# Revit family: Hager-Univers-IP65-D300-H550-Cl.II-encl-PT-pt
name_source: partatom
category: Equipement électrique
units: mm (PartAtom-declared; Revit-internal decimal feet)

## family parameters
Configuration du panneau = Deux colonnes, circuits au sein
Cote de connecteur circulaire = Utiliser le diamètre
Couper avec des vides une fois chargée = Non
Hôte = Face
Partagée = Non
Point de calcul de pièce = Non
Type d'élément = Tableau de raccordement

## types (6) — shared parameters
Commentaires du type = Univers
EF000003 - Método de montagem = EV000384 - Montagem em superfície (gesso)
EF000007 - Cor = EV000270 - Cinzento
EF000040 - Altura = 550 mm
EF000049 - Profundidade = 300 mm  [stored 0.984252 ft]
EF000116 - Número RAL = 7035
EF000118 - Com tampa de montagem = Non
EF000266 - Número de linhas = 3
EF001088 - Extensão possível = Non
EF001131 - Profundidade interior = 150 mm  [stored 0.492126 ft]
EF001596 - Material do corpo = EV000139 - Plástico
EF001613 - Integridade do circuito = EV000494 - Nenhum
EF003532 - Adequado para uso no exterior = Oui
EF004293 - Força de impacto = EV008784 - IK10
EF004464 - Tipo de porta = EV002646 - Único
EF005474 - Grau de proteção (IP) = EV006421 - IP65
EF006244 - Tampa/porta transparente = Non
EF006306 - Com fecho = Oui
EF007800 - Adequado para proteção contra raios = Oui
EF009170 - Espessura do material do invólucro = 2 mm  [stored 0.00656168 ft]
EF009171 - Espessura do material da porta/tampa = 2 mm  [stored 0.00656168 ft]
EF009212 - Tipo de tampa = EV000116 - Fechado
EF015940 - Tampa com libertação de sobrepressão = Non
Fabricant = Hager
HG000002 - Com porta ou tampa = Oui
HG000003 - Gama = Univers
HG000006 - Encastrado = Non
HG000009 - Porta dupla = Non
HG000010 - Portas assimétricas = Non
HG000023 - Recinto de secção dupla = Non
HG000024 - Altura da secção inferior = 800 mm
HG000026 - Instalação no chão = Non
zero-valued in all types: EF000218 - Profundidade incorporada, EF000437 - Número de entradas de condutores, EF009554 - Número de aberturas para placas de flange, Elévation par défaut, HG000027 - Altura da Plinta

## per-type parameters (varying)
| type | EF000008 - Largura | EF000339 - Tipo de difusor | EF002950 - Largura em número de módulos | EF004427 - Número de módulos | EF008873 - Corrente nominal (In) | HG000004 - Referência do Fabricante |
| Montagem em superfície (gesso) IP65 L1100 A550 P300  - FL34S | 1100 mm | EV001012 - Tampa | 48 | 144 | 630 A | FL34S |
| Montagem em superfície (gesso) IP65 L1100 A550 P300  - FL34SP | 1100 mm | EV001012 - Tampa | 48 | 144 | 630 A | FL34SP |
| Montagem em superfície (gesso) IP65 L600 A550 P300  - FL32S | 600 mm | EV004216 - Porta | 24 | 72 | 400 A | FL32S |
| Montagem em superfície (gesso) IP65 L600 A550 P300  - FL32SP | 600 mm | EV004216 - Porta | 24 | 72 | 400 A | FL32SP |
| Montagem em superfície (gesso) IP65 L850 A550 P300  - FL33S | 850 mm  [stored 2.78871 ft] | EV004216 - Porta | 36 | 108 | 630 A | FL33S |
| Montagem em superfície (gesso) IP65 L850 A550 P300  - FL33SP | 850 mm  [stored 2.78871 ft] | EV004216 - Porta | 36 | 108 | 630 A | FL33SP |

note: [stored X ft] marks values corroborated as IEEE doubles in the binary element streams (Revit-internal decimal feet)

## geometry (parser evidence)
native form markers: Sweep x10
no freeform markers — native parametric forms only
